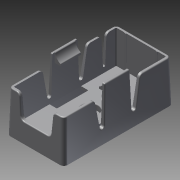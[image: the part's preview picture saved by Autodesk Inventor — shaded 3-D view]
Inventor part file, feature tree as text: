
AUTODESK INVENTOR PART (.ipt)
format: ipt  version: 2013 (Build 170138000, 138)  size: 531,456 bytes
history: native  units: in
note: dims shown in document units (in); Inventor stores cm internally (conversion verified against a paired STEP export)
features: sketch x12, extrude x11, fillet x8, plane x7, mirror x2, loft x1, hole x1, other x1, projected_geometry x1
ambient origin geometry x8: Origin, YZ Plane, XZ Plane, XY Plane, X Axis, Y Axis, Z Axis, Center Point
bodies: Solid1 (feature_tree)
feature tree (44):
  extrude  "Extrusion1"  Depth=0.079in
  fillet  "Fillet1"  [1 undecoded]
  plane  "Work Plane1"
  extrude  "Extrusion2"  Depth=0.02in
  fillet  "Fillet2"  [1 undecoded]
  plane  "Work Plane2"
  extrude  "Extrusion3"  Depth=0.079in
  fillet  "Fillet3"  [1 undecoded]
  plane  "Work Plane3"
  extrude  "Extrusion4"  Depth=0.079in
  fillet  "Fillet4"  Radius=0.894in
  plane  "Work Plane4"
  sketch  "Sketch5"  dims[d16=0.0in d17=90.0deg d18=0.0in d19=90.0deg]
  sketch  "Sketch6"  dims[d21=0.433in d22=0.0in d23=0.433in d24=0.0in]
  loft  "Loft1"
  mirror  "Mirror1"
  plane  "Work Plane5"
  sketch  "Sketch7"  dims[d25=0.118in d26=0.0in d27=0.335in]
  extrude  "Extrusion5"  Depth=0.433in TaperAngle=0.0deg
  extrude  "Extrusion6"  Depth=0.335in
  mirror  "Mirror2"
  sketch  "Sketch8"  dims[d28=0.118in d29=0.0in]
  extrude  "Extrusion7"  Depth=0.02in
  extrude  "Extrusion8"  Depth=0.4375in TaperAngle=0.0deg
  hole  "Hole1"  [1 undecoded]
  fillet  "Fillet6"  Radius=0.02in
  plane  "Work Plane6"
  extrude  "Extrusion9"  Depth=0.1875in TaperAngle=0.0deg
  fillet  "Fillet7"  Radius=0.5625in
  fillet  "Fillet8"  [1 undecoded]
  fillet  "Fillet9"  [1 undecoded]
  extrude  "Extrusion10"  [1 undecoded]
  extrude  "Extrusion11"  [1 undecoded]
  plane  "Work Plane7"
  sketch  "Sketch1"  dims[d0=0.874in d1=-0.0103in d2=0.079in d3=-0.697in]
  sketch  "Sketch2"  dims[d4=0.751in d5=0.0034in d6=0.02in d7=0.0in]
  sketch  "Sketch3"  dims[d8=0.3115in d9=0.0in d10=0.079in d11=0.0in]
  sketch  "Sketch4"  dims[d12=0.751in d13=0.0in d14=0.079in d15=0.894in]
  other  "Edges1"
  sketch  "Sketch9"  dims[d30=0.177in d31=0.75in d32=0.375in d33=0.25in d34=0.5635in d35=1.0in d36=0.8108in d37=0.02in]
  sketch  "Sketch10"  dims[d38=0.0in d39=0.4375in d40=0.0in]
  sketch  "Sketch11"  dims[d41=0.079in d42=0.02in d43=0.02in]
  sketch  "Sketch12"  dims[d44=0.02in d45=0.1875in d46=0.0in d47=0.5625in d48=0.0in]
  projected_geometry  "Project Cut Edges1"
note: 8 required parameter values undecoded (feature->parameter linkage not recoverable at this tier; creation-order binding heuristic only, values carry confidence <= 0.55)
